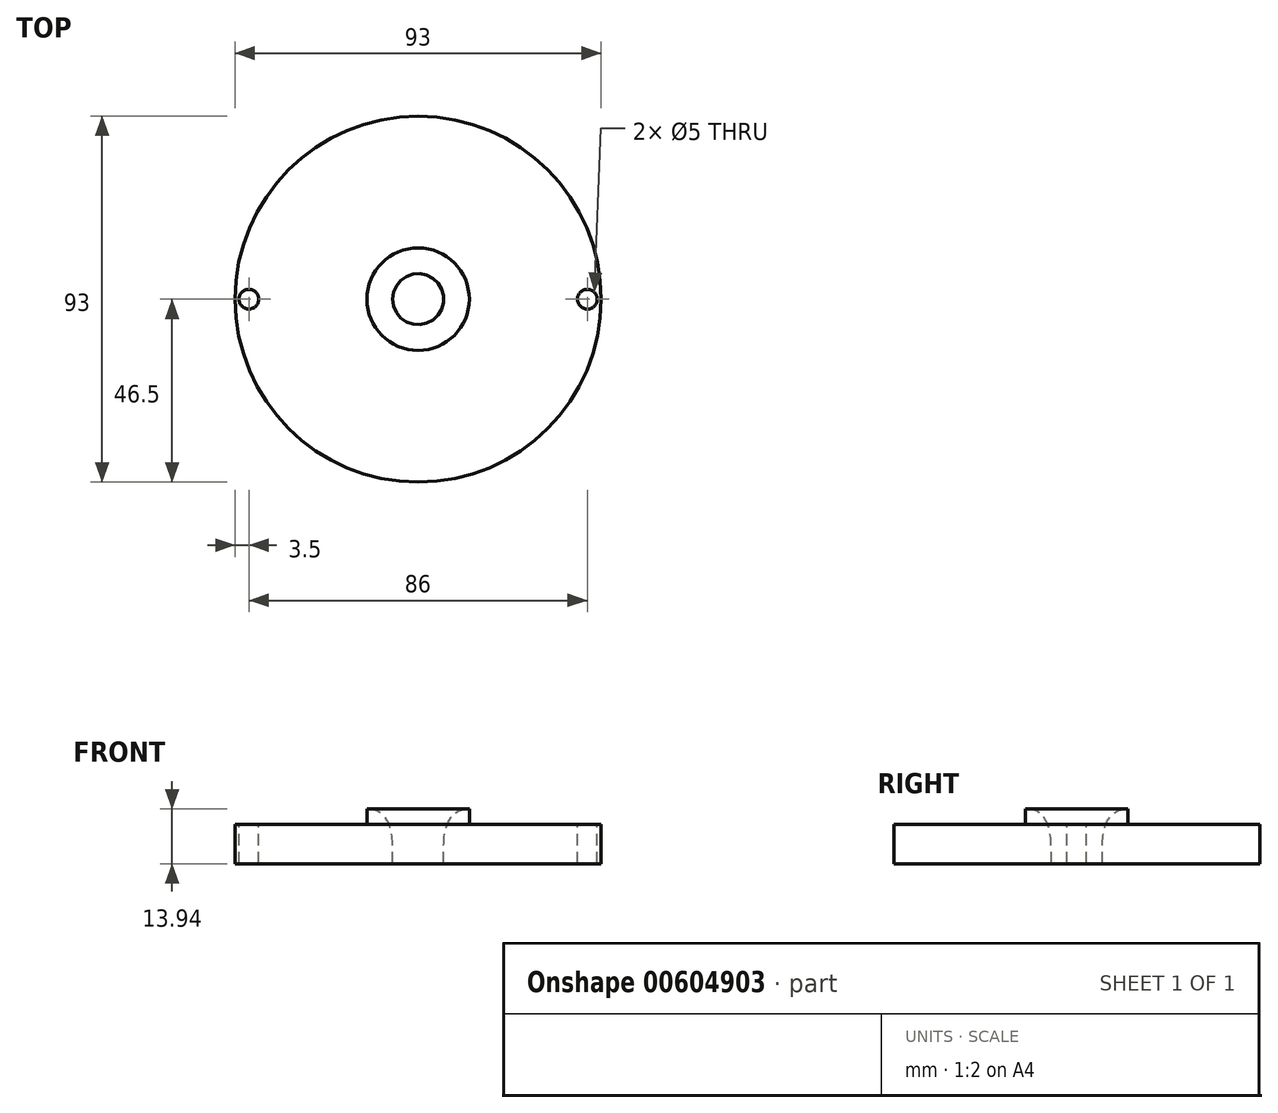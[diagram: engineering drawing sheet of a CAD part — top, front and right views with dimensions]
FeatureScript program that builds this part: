
annotation { "Feature Type Name" : "Feature", "Feature Type Description" : "" }
export const myFeature = defineFeature(function(context is Context, id is Id, definition is map)
    precondition{}
    {
        {
            var Q0;
            Q0=qCreatedBy(makeId("Front.planeOp"),FACE);
            var sketch = newSketch(context, id + "F0", { "sketchPlane" : qUnion([Q0])});
            skLineSegment(sketch, "E0", {"start": v(6.5, 1.8) * mm, "end": v(46.5, 1.8) * mm});
            skLineSegment(sketch, "E1", {"start": v(46.5, 1.8) * mm, "end": v(46.5, 11.8) * mm});
            skLineSegment(sketch, "E2", {"start": v(46.5, 11.8) * mm, "end": v(14.93, 11.8) * mm});
            skLineSegment(sketch, "E3", {"start": v(0, 0) * mm, "end": v(0, 23.95) * mm});
            skLineSegment(sketch, "E4", {"start": v(13, 12.74) * mm, "end": v(13, 15.74) * mm});
            skFitSpline(sketch, "E5", {"points": [v(6.5, 1.8) * mm, v(7.1, 11.01) * mm, v(13, 15.74) * mm], "startDerivative": vector(0, 21.05) * mm, "endDerivative": vector(23.17, 0.44) * mm});
            skLineSegment(sketch, "E6", {"start": v(13, 12.74) * mm, "end": v(13, 11.8) * mm});
            skLineSegment(sketch, "E7", {"start": v(13, 11.8) * mm, "end": v(14.93, 11.8) * mm});
            skSolve(sketch);
        }
        {
            var Q0;
            Q0=makeQuery(id+"F0.imprint","IMPRINT",FACE,{"disambiguationData":[TD([[makeQuery(id+"F0.imprint","IMPRINT",EDGE,{"derivedFrom":sQuery(id+"F0.wireOp",EDGE,"E0")}),1.0]])]});
            var Q1;
            Q1=sQuery(id+"F0.wireOp",EDGE,"E3");
            revolve(context, id + "F1", {"entities" : qUnion([Q0]), "axis" : qUnion([Q1]), "revolveType" : RevolveType.FULL});
        }
        {
            var Q0;
            Q0=makeQuery(id+"F1.opRevolve","SWEPT_FACE",FACE,{"disambiguationData":[OSD([sQuery(id+"F0.wireOp",EDGE,"E2"),sQuery(id+"F0.wireOp",EDGE,"E7")])]});
            var sketch = newSketch(context, id + "F2", { "sketchPlane" : qUnion([Q0])});
            skCircle(sketch, "E8", {"center": v(43, 0) * mm, "radius": 2.5 * mm});
            skCircle(sketch, "E9", {"center": v(-43, 0) * mm, "radius": 2.5 * mm});
            skSolve(sketch);
        }
        {
            var Q0;
            Q0=sQuery(id+"F2.wireOp",VERTEX,"E9.center");
            var Q1;
            Q1=sQuery(id+"F2.wireOp",VERTEX,"E8.center");
            var Q2;
            Q2=makeQuery(id+"F1.opRevolve","SWEPT_BODY",BODY,{"disambiguationData":[OSD([sQuery(id+"F0.wireOp",EDGE,"E0"),sQuery(id+"F0.wireOp",EDGE,"E1"),sQuery(id+"F0.wireOp",EDGE,"E2"),sQuery(id+"F0.wireOp",EDGE,"E4"),sQuery(id+"F0.wireOp",EDGE,"E5"),sQuery(id+"F0.wireOp",EDGE,"E6"),sQuery(id+"F0.wireOp",EDGE,"E7")])]});
            hole(context, id + "F3", {"style" : HoleStyle.SIMPLE, "endStyle" : HoleEndStyle.THROUGH, "holeDiameter" : 5 * mm, "majorDiameter" : 5 * mm, "isTappedThrough" : true, "tappedDepth" : 12 * mm, "tapClearance" : 3, "locations" : qUnion([Q0, Q1]), "scope" : qUnion([Q2])});
        }
    });
